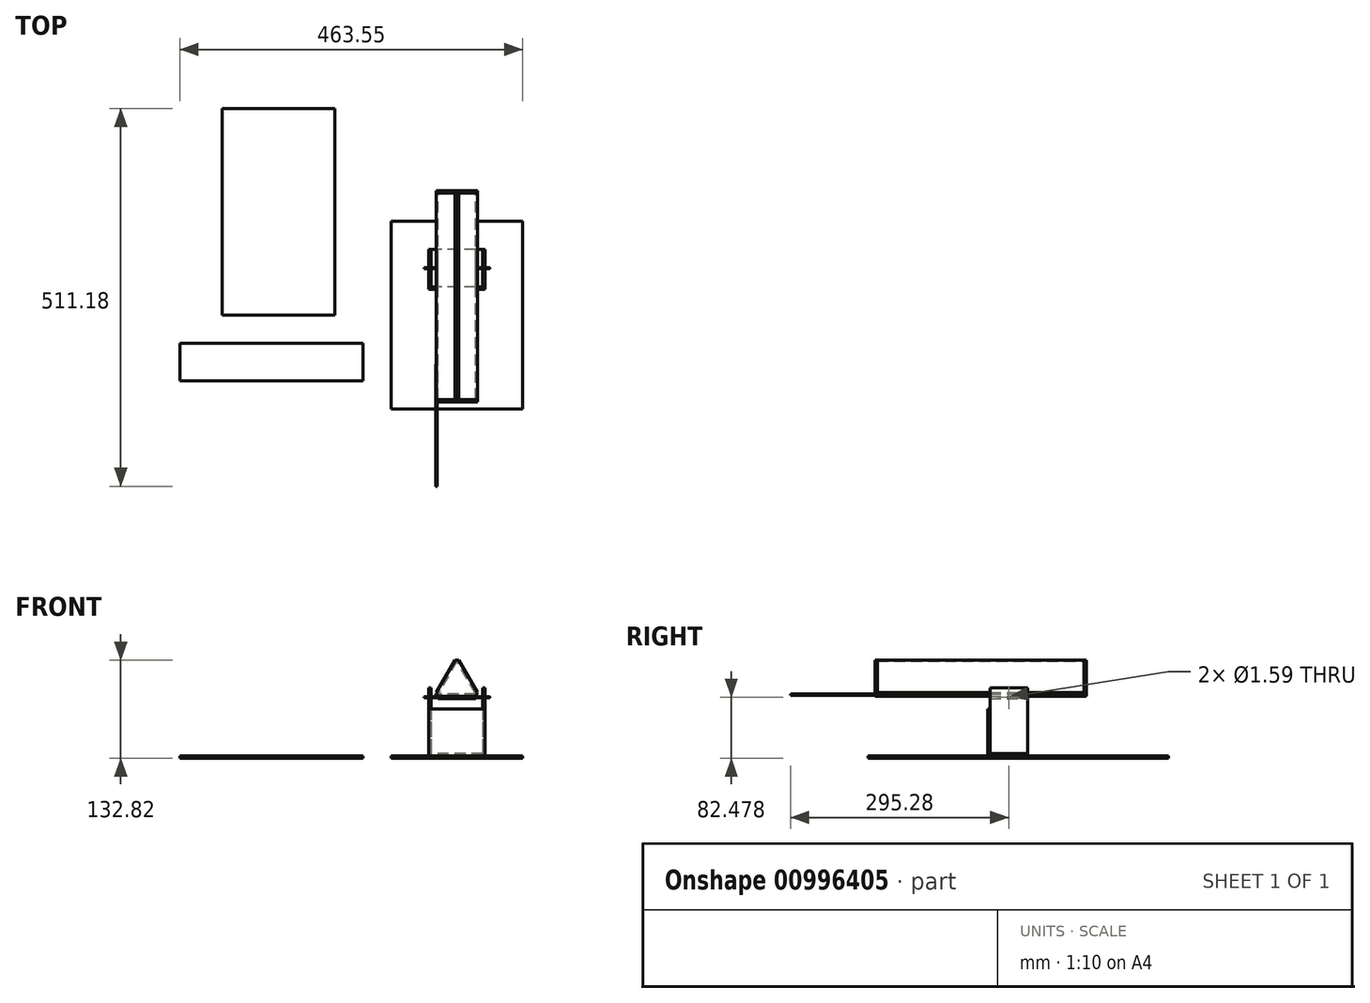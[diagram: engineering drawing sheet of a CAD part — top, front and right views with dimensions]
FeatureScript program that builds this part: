
annotation { "Feature Type Name" : "Feature", "Feature Type Description" : "" }
export const myFeature = defineFeature(function(context is Context, id is Id, definition is map)
    precondition{}
    {
        {
            var Q0;
            Q0=qCreatedBy(makeId("Top.planeOp"),FACE);
            var sketch = newSketch(context, id + "F0", { "sketchPlane" : qUnion([Q0])});
            skLineSegment(sketch, "E0.bottom", {"start": v(88.9, -127) * mm, "end": v(-88.9, -127) * mm});
            skLineSegment(sketch, "E0.top", {"start": v(88.9, 127) * mm, "end": v(-88.9, 127) * mm});
            skLineSegment(sketch, "E0.left", {"start": v(88.9, -127) * mm, "end": v(88.9, 127) * mm});
            skLineSegment(sketch, "E0.right", {"start": v(-88.9, -127) * mm, "end": v(-88.9, 127) * mm});
            skPoint(sketch, "E0.middle", {"position": v(0, 0) * mm});
            skSolve(sketch);
        }
        {
            var Q0;
            Q0 = qSketchRegion(id + "F0", true);
            extrude(context, id + "F1", {"entities" : qUnion([Q0]), "depth" : 3.17 * mm, "offsetDistance" : 25.4 * mm});
        }
        {
            var Q0;
            Q0=makeQuery(id+"F1.opExtrude","CAP_FACE",FACE,{"disambiguationData":[OSD([sQuery(id+"F0.wireOp",EDGE,"E0.bottom"),sQuery(id+"F0.wireOp",EDGE,"E0.top"),sQuery(id+"F0.wireOp",EDGE,"E0.left"),sQuery(id+"F0.wireOp",EDGE,"E0.right")])],"isStart":false});
            var sketch = newSketch(context, id + "F2", { "sketchPlane" : qUnion([Q0])});
            skLineSegment(sketch, "E1.bottom", {"start": v(34.92, 38.1) * mm, "end": v(-34.93, 38.1) * mm});
            skLineSegment(sketch, "E1.top", {"start": v(34.92, 88.9) * mm, "end": v(-34.93, 88.9) * mm});
            skLineSegment(sketch, "E1.left", {"start": v(34.92, 38.1) * mm, "end": v(34.92, 88.9) * mm});
            skLineSegment(sketch, "E1.right", {"start": v(-34.93, 38.1) * mm, "end": v(-34.93, 88.9) * mm});
            skPoint(sketch, "E1.middle", {"position": v(0, 63.5) * mm});
            skSolve(sketch);
        }
        {
            var Q0;
            Q0 = qSketchRegion(id + "F2", true);
            extrude(context, id + "F3", {"entities" : qUnion([Q0]), "depth" : 3.17 * mm, "offsetDistance" : 25.4 * mm});
        }
        {
            var Q0;
            Q0=makeQuery(id+"F3.opExtrude","CAP_FACE",FACE,{"disambiguationData":[OSD([sQuery(id+"F2.wireOp",EDGE,"E1.bottom"),sQuery(id+"F2.wireOp",EDGE,"E1.top"),sQuery(id+"F2.wireOp",EDGE,"E1.left"),sQuery(id+"F2.wireOp",EDGE,"E1.right")])],"isStart":false});
            var sketch = newSketch(context, id + "F4", { "sketchPlane" : qUnion([Q0])});
            skLineSegment(sketch, "E2.bottom", {"start": v(34.92, 88.9) * mm, "end": v(38.1, 88.9) * mm});
            skLineSegment(sketch, "E2.top", {"start": v(34.92, 38.1) * mm, "end": v(38.1, 38.1) * mm});
            skLineSegment(sketch, "E2.left", {"start": v(34.92, 88.9) * mm, "end": v(34.92, 38.1) * mm});
            skLineSegment(sketch, "E2.right", {"start": v(38.1, 88.9) * mm, "end": v(38.1, 38.1) * mm});
            skLineSegment(sketch, "E3.bottom", {"start": v(-34.93, 88.9) * mm, "end": v(-38.1, 88.9) * mm});
            skLineSegment(sketch, "E3.top", {"start": v(-34.93, 38.1) * mm, "end": v(-38.1, 38.1) * mm});
            skLineSegment(sketch, "E3.left", {"start": v(-34.93, 88.9) * mm, "end": v(-34.93, 38.1) * mm});
            skLineSegment(sketch, "E3.right", {"start": v(-38.1, 88.9) * mm, "end": v(-38.1, 38.1) * mm});
            skSolve(sketch);
        }
        {
            var Q0;
            Q0 = qSketchRegion(id + "F4", true);
            extrude(context, id + "F5", {"entities" : qUnion([Q0]), "depth" : 88.9 * mm, "offsetDistance" : 25.4 * mm});
        }
        {
            var Q0;
            Q0=makeQuery(id+"F5.opExtrude","SWEPT_FACE",FACE,{"disambiguationData":[OSD([sQuery(id+"F4.wireOp",EDGE,"E3.right")])]});
            var sketch = newSketch(context, id + "F6", { "sketchPlane" : qUnion([Q0])});
            skCircle(sketch, "E4", {"center": v(-63.5, 82.48) * mm, "radius": 0.8 * mm});
            skPoint(sketch, "E4.centerSnap0", {"position": v(-63.5, 95.25) * mm});
            skSolve(sketch);
        }
        {
            var Q0;
            Q0 = qSketchRegion(id + "F6", true);
            extrude(context, id + "F7", {"entities" : qUnion([Q0]), "operationType" : NewBodyOperationType.REMOVE, "endBound" : BoundingType.THROUGH_ALL, "oppositeDirection" : true, "depth" : 25.4 * mm, "offsetDistance" : 25.4 * mm});
        }
        {
            var Q0;
            Q0=makeQuery(id+"F5.opExtrude","SWEPT_FACE",FACE,{"disambiguationData":[OSD([sQuery(id+"F4.wireOp",EDGE,"E3.right")])]});
            var sketch = newSketch(context, id + "F8", { "sketchPlane" : qUnion([Q0])});
            skCircle(sketch, "E5.0", {"center": v(-63.5, 82.48) * mm, "radius": 0.8 * mm});
            skSolve(sketch);
        }
        {
            var Q0;
            Q0 = qSketchRegion(id + "F8", true);
            var Q1;
            Q1=makeQuery(id+"F5.opExtrude","SWEPT_FACE",FACE,{"disambiguationData":[OSD([sQuery(id+"F4.wireOp",EDGE,"E2.right")])]});
            extrude(context, id + "F9", {"entities" : qUnion([Q0]), "depth" : 6.35 * mm, "offsetDistance" : 25.4 * mm, "hasSecondDirection" : true, "secondDirectionBound" : SecondDirectionBoundingType.UP_TO_SURFACE, "secondDirectionOppositeDirection" : true, "secondDirectionDepth" : 25.4 * mm, "secondDirectionBoundEntityFace" : qUnion([Q1]), "hasSecondDirectionOffset" : true, "secondDirectionOffsetDistance" : 6.35 * mm, "secondDirectionOffsetOppositeDirection" : true});
        }
        {
            var Q0;
            Q0=qCreatedBy(makeId("Right.planeOp"),FACE);
            var sketch = newSketch(context, id + "F10", { "sketchPlane" : qUnion([Q0])});
            skLineSegment(sketch, "E6.bottom", {"start": v(38.1, 80.89) * mm, "end": v(88.9, 80.89) * mm});
            skLineSegment(sketch, "E6.top", {"start": v(38.1, 84.06) * mm, "end": v(88.9, 84.06) * mm});
            skLineSegment(sketch, "E6.left", {"start": v(38.1, 80.89) * mm, "end": v(38.1, 84.06) * mm});
            skLineSegment(sketch, "E6.right", {"start": v(88.9, 80.89) * mm, "end": v(88.9, 84.06) * mm});
            skPoint(sketch, "E6.middle", {"position": v(63.5, 82.48) * mm});
            skSolve(sketch);
        }
        {
            var Q0;
            Q0 = qSketchRegion(id + "F10", true);
            extrude(context, id + "F11", {"entities" : qUnion([Q0]), "endBound" : BoundingType.SYMMETRIC, "depth" : 50.8 * mm, "offsetDistance" : 25.4 * mm});
        }
        {
            var Q0;
            Q0=makeQuery(id+"F11.opExtrude","SWEPT_FACE",FACE,{"disambiguationData":[OSD([sQuery(id+"F10.wireOp",EDGE,"E6.right")])]});
            cPlane(context, id + "F12", {"entities" : qUnion([Q0]), "cplaneType" : CPlaneType.OFFSET, "offset" : 76.2 * mm, "width" : 152.4 * mm, "height" : 152.4 * mm});
        }
        {
            var Q0;
            Q0=qCreatedBy(id+"F12.planeOp",FACE);
            var sketch = newSketch(context, id + "F13", { "sketchPlane" : qUnion([Q0])});
            skLineSegment(sketch, "E7.0", {"start": v(-25.4, 84.06) * mm, "end": v(25.4, 84.06) * mm, "construction": true});
            skLineSegment(sketch, "E8.bottom", {"start": v(-25.4, 84.06) * mm, "end": v(25.4, 84.06) * mm});
            skLineSegment(sketch, "E8.top", {"start": v(-25.4, 87.24) * mm, "end": v(25.4, 87.24) * mm});
            skLineSegment(sketch, "E8.left", {"start": v(-25.4, 84.06) * mm, "end": v(-25.4, 87.24) * mm});
            skLineSegment(sketch, "E8.right", {"start": v(25.4, 84.06) * mm, "end": v(25.4, 87.24) * mm});
            skLineSegment(sketch, "E9", {"start": v(-25.4, 87.24) * mm, "end": v(0, 131.23) * mm});
            skLineSegment(sketch, "E10", {"start": v(0, 131.23) * mm, "end": v(25.4, 87.24) * mm});
            skLineSegment(sketch, "E11.0", {"start": v(2.75, 132.82) * mm, "end": v(28.15, 88.83) * mm});
            skLineSegment(sketch, "E12.0", {"start": v(-28.15, 88.83) * mm, "end": v(-2.75, 132.82) * mm});
            skLineSegment(sketch, "E13", {"start": v(0, 131.23) * mm, "end": v(2.75, 132.82) * mm});
            skLineSegment(sketch, "E14", {"start": v(25.4, 87.24) * mm, "end": v(28.15, 88.83) * mm});
            skLineSegment(sketch, "E15", {"start": v(-2.75, 132.82) * mm, "end": v(0, 131.23) * mm});
            skLineSegment(sketch, "E16", {"start": v(-28.15, 88.83) * mm, "end": v(-25.4, 87.24) * mm});
            skSolve(sketch);
        }
        {
            var Q0;
            Q0=makeQuery(id+"F13.imprint","IMPRINT",FACE,{"disambiguationData":[TD([[makeQuery(id+"F13.imprint","IMPRINT",EDGE,{"derivedFrom":sQuery(id+"F13.wireOp",EDGE,"E9")}),1.0]])]});
            var Q1;
            Q1=makeQuery(id+"F13.imprint","IMPRINT",FACE,{"disambiguationData":[TD([[makeQuery(id+"F13.imprint","IMPRINT",EDGE,{"derivedFrom":sQuery(id+"F13.wireOp",EDGE,"E10")}),1.0]])]});
            var Q2;
            Q2=makeQuery(id+"F13.imprint","IMPRINT",FACE,{"disambiguationData":[TD([[makeQuery(id+"F13.imprint","IMPRINT",EDGE,{"derivedFrom":sQuery(id+"F13.wireOp",EDGE,"E8.bottom")}),1.0]])]});
            extrude(context, id + "F14", {"entities" : qUnion([Q0, Q1, Q2]), "oppositeDirection" : true, "depth" : 279.4 * mm, "offsetDistance" : 25.4 * mm});
        }
        {
            var Q0;
            Q0=makeQuery(id+"F14.opExtrude","CAP_FACE",FACE,{"disambiguationData":[OSD([sQuery(id+"F13.wireOp",EDGE,"E9"),sQuery(id+"F13.wireOp",EDGE,"E12.0"),sQuery(id+"F13.wireOp",EDGE,"E15"),sQuery(id+"F13.wireOp",EDGE,"E16")])],"isStart":true});
            var Q1;
            Q1=makeQuery(id+"F14.opExtrude","CAP_FACE",FACE,{"disambiguationData":[OSD([sQuery(id+"F13.wireOp",EDGE,"E9"),sQuery(id+"F13.wireOp",EDGE,"E12.0"),sQuery(id+"F13.wireOp",EDGE,"E15"),sQuery(id+"F13.wireOp",EDGE,"E16")])],"isStart":false});
            cPlane(context, id + "F15", {"entities" : qUnion([Q0, Q1]), "cplaneType" : CPlaneType.MID_PLANE, "offset" : 25.4 * mm, "width" : 152.4 * mm, "height" : 152.4 * mm});
        }
        {
            var Q0;
            Q0=makeQuery(id+"F14.opExtrude","CAP_FACE",FACE,{"disambiguationData":[OSD([sQuery(id+"F13.wireOp",EDGE,"E9"),sQuery(id+"F13.wireOp",EDGE,"E12.0"),sQuery(id+"F13.wireOp",EDGE,"E15"),sQuery(id+"F13.wireOp",EDGE,"E16")])],"isStart":true});
            var sketch = newSketch(context, id + "F16", { "sketchPlane" : qUnion([Q0])});
            skLineSegment(sketch, "E17.0", {"start": v(-28.15, 88.83) * mm, "end": v(-2.75, 132.82) * mm});
            skLineSegment(sketch, "E18.0", {"start": v(2.75, 132.82) * mm, "end": v(28.15, 88.83) * mm});
            skLineSegment(sketch, "E19.0", {"start": v(-25.4, 84.06) * mm, "end": v(25.4, 84.06) * mm});
            skLineSegment(sketch, "E20", {"start": v(-2.75, 132.82) * mm, "end": v(2.75, 132.82) * mm});
            skLineSegment(sketch, "E21", {"start": v(-28.15, 88.83) * mm, "end": v(-25.4, 84.06) * mm});
            skLineSegment(sketch, "E22", {"start": v(25.4, 84.06) * mm, "end": v(28.15, 88.83) * mm});
            skSolve(sketch);
        }
        {
            var Q0;
            Q0 = qSketchRegion(id + "F16", true);
            extrude(context, id + "F17", {"entities" : qUnion([Q0]), "depth" : 3.17 * mm, "offsetDistance" : 25.4 * mm});
        }
        {
            var Q0;
            Q0=makeQuery(id+"F17.opExtrude","SWEPT_BODY",BODY,{"disambiguationData":[OSD([sQuery(id+"F16.wireOp",EDGE,"E17.0"),sQuery(id+"F16.wireOp",EDGE,"E18.0"),sQuery(id+"F16.wireOp",EDGE,"E19.0"),sQuery(id+"F16.wireOp",EDGE,"E20"),sQuery(id+"F16.wireOp",EDGE,"E21"),sQuery(id+"F16.wireOp",EDGE,"E22")])]});
            var Q1;
            Q1=qCreatedBy(id+"F15.planeOp",FACE);
            mirror(context, id + "F18", {"entities" : qUnion([Q0]), "mirrorPlane" : qUnion([Q1])});
        }
        {
            var Q0;
            Q0=makeQuery(id+"F18.opPattern","COPY",FACE,{"derivedFrom":makeQuery(id+"F17.opExtrude","CAP_FACE",FACE,{"disambiguationData":[OSD([sQuery(id+"F16.wireOp",EDGE,"E17.0"),sQuery(id+"F16.wireOp",EDGE,"E18.0"),sQuery(id+"F16.wireOp",EDGE,"E19.0"),sQuery(id+"F16.wireOp",EDGE,"E20"),sQuery(id+"F16.wireOp",EDGE,"E21"),sQuery(id+"F16.wireOp",EDGE,"E22")])],"isStart":false}),"instanceName":"1"});
            var sketch = newSketch(context, id + "F19", { "sketchPlane" : qUnion([Q0])});
            skLineSegment(sketch, "E23", {"start": v(-26.77, 86.45) * mm, "end": v(-27.46, 86.05) * mm, "construction": true});
            skCircle(sketch, "E24", {"center": v(-27.46, 86.05) * mm, "radius": 0.8 * mm});
            skSolve(sketch);
        }
        {
            var Q0;
            Q0 = qSketchRegion(id + "F19", true);
            extrude(context, id + "F20", {"entities" : qUnion([Q0]), "operationType" : NewBodyOperationType.ADD, "oppositeDirection" : true, "depth" : 50.8 * mm, "offsetDistance" : 25.4 * mm, "hasSecondDirection" : true, "secondDirectionOppositeDirection" : false, "secondDirectionDepth" : 114.3 * mm});
        }
        {
            var Q0;
            Q0=qCreatedBy(makeId("Top.planeOp"),FACE);
            var sketch = newSketch(context, id + "F21", { "sketchPlane" : qUnion([Q0])});
            skLineSegment(sketch, "E25.bottom", {"start": v(-165.1, 0) * mm, "end": v(-317.5, 0) * mm});
            skLineSegment(sketch, "E25.top", {"start": v(-165.1, 279.4) * mm, "end": v(-317.5, 279.4) * mm});
            skLineSegment(sketch, "E25.left", {"start": v(-165.1, 0) * mm, "end": v(-165.1, 279.4) * mm});
            skLineSegment(sketch, "E25.right", {"start": v(-317.5, 0) * mm, "end": v(-317.5, 279.4) * mm});
            skSolve(sketch);
        }
        {
            var Q0;
            Q0 = qSketchRegion(id + "F21", true);
            extrude(context, id + "F22", {"entities" : qUnion([Q0]), "depth" : 3.17 * mm, "offsetDistance" : 25.4 * mm});
        }
        {
            var Q0;
            Q0=makeQuery(id+"F5.opExtrude","SWEPT_FACE",FACE,{"disambiguationData":[OSD([sQuery(id+"F4.wireOp",EDGE,"E2.top")])]});
            var sketch = newSketch(context, id + "F23", { "sketchPlane" : qUnion([Q0])});
            skLineSegment(sketch, "E26.bottom", {"start": v(-38.1, 3.18) * mm, "end": v(38.1, 3.18) * mm});
            skLineSegment(sketch, "E26.top", {"start": v(-38.1, 66.67) * mm, "end": v(38.1, 66.67) * mm});
            skLineSegment(sketch, "E26.left", {"start": v(-38.1, 3.17) * mm, "end": v(-38.1, 66.67) * mm});
            skLineSegment(sketch, "E26.right", {"start": v(38.1, 3.18) * mm, "end": v(38.1, 66.67) * mm});
            skSolve(sketch);
        }
        {
            var Q0;
            Q0 = qSketchRegion(id + "F23", true);
            extrude(context, id + "F24", {"entities" : qUnion([Q0]), "depth" : 3.17 * mm, "offsetDistance" : 25.4 * mm});
        }
        {
            var Q0;
            Q0=qCreatedBy(makeId("Top.planeOp"),FACE);
            var sketch = newSketch(context, id + "F25", { "sketchPlane" : qUnion([Q0])});
            skLineSegment(sketch, "E27.bottom", {"start": v(-127, -88.9) * mm, "end": v(-374.65, -88.9) * mm});
            skLineSegment(sketch, "E27.top", {"start": v(-127, -38.1) * mm, "end": v(-374.65, -38.1) * mm});
            skLineSegment(sketch, "E27.left", {"start": v(-127, -88.9) * mm, "end": v(-127, -38.1) * mm});
            skLineSegment(sketch, "E27.right", {"start": v(-374.65, -88.9) * mm, "end": v(-374.65, -38.1) * mm});
            skSolve(sketch);
        }
        {
            var Q0;
            Q0 = qSketchRegion(id + "F25", true);
            extrude(context, id + "F26", {"entities" : qUnion([Q0]), "depth" : 3.17 * mm, "offsetDistance" : 25.4 * mm});
        }
    });
